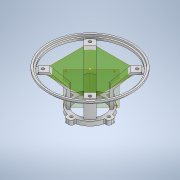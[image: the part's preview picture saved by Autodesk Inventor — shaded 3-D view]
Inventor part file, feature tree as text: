
AUTODESK INVENTOR PART (.ipt)
format: ipt  version: 2020 (Build 240168000, 168)  size: 382,976 bytes
history: native  units: mm
features: other x11, sketch x7, revolve x4, extrude x3, projected_geometry x3, pattern_circular x1
ambient origin geometry x8: Origin, YZ Plane, XZ Plane, XY Plane, X Axis, Y Axis, Z Axis, Center Point
bodies: Body1 (feature_tree)
feature tree (29):
  other  "Твердое тело1"
  extrude  "Выдавливание1"  Depth=34.0mm
  other  "РабПлоскость1"
  other  "РабОсь1"
  revolve  "Вращение1"
  sketch  "Эскиз3"
  other  "РабТочка1"
  extrude  "Выдавливание2"  Depth=45.0mm
  other  "РабТочка2"
  other  "РабТочка3"
  other  "РабТочка4"
  other  "РабПлоскость2"
  sketch  "Эскиз5"
  revolve  "Вращение2"
  revolve  "Вращение3"
  pattern_circular  "Круговой массив1"  Angle=45.0deg  [1 undecoded]
  extrude  "Выдавливание3"  Depth=3.3mm
  revolve  "Вращение4"
  sketch  "Эскиз1"
  sketch  "Эскиз2"
  sketch  "Эскиз4"
  projected_geometry  "Спроецированная петля1"
  projected_geometry  "Спроецированная петля2"
  projected_geometry  "Спроецированная петля3"
  other  "РабПлоскость3"
  other  "РабПлоскость4"
  other  "РабПлоскость5"
  sketch  "Эскиз6"
  sketch  "Эскиз7"
note: 1 required parameter value undecoded (feature->parameter linkage not recoverable at this tier; creation-order binding heuristic only, values carry confidence <= 0.55)
